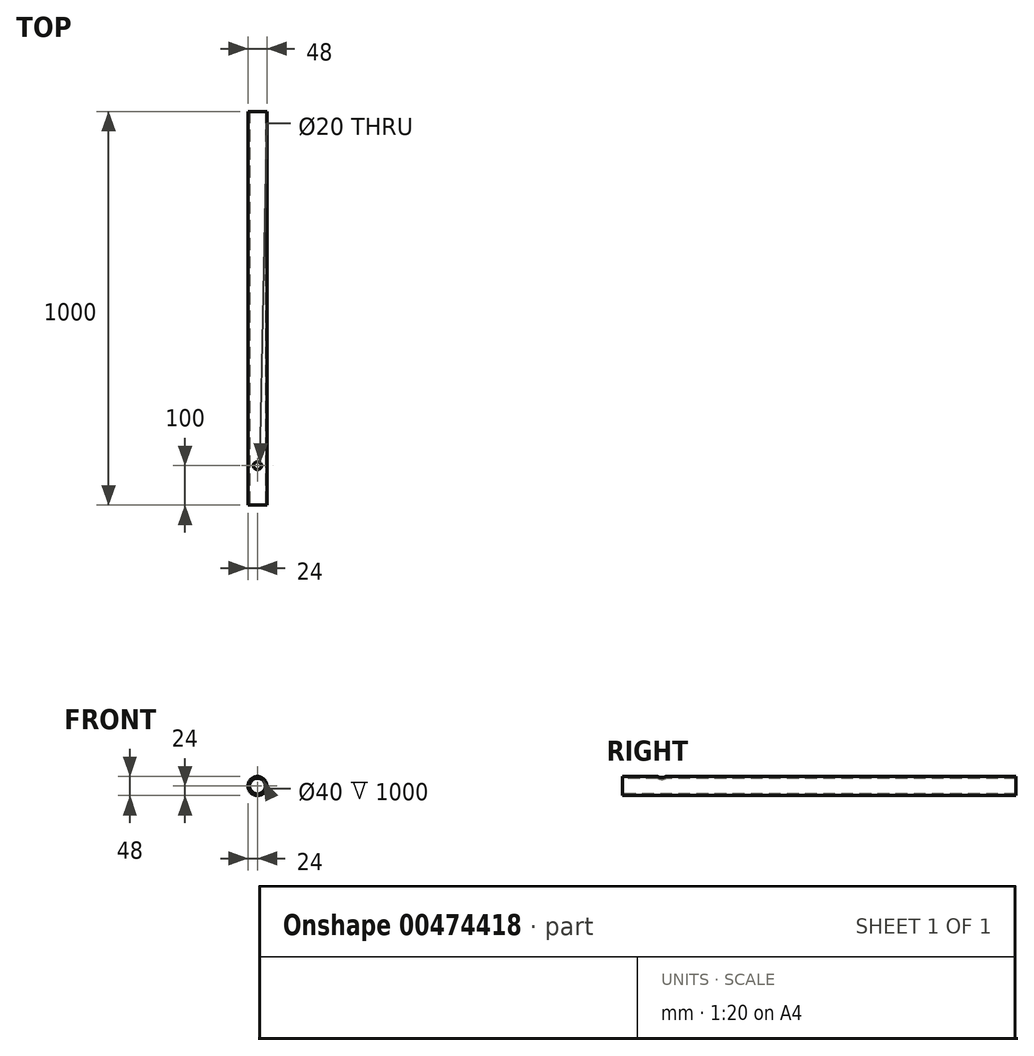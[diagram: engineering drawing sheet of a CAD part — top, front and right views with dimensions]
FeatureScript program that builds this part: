
annotation { "Feature Type Name" : "Feature", "Feature Type Description" : "" }
export const myFeature = defineFeature(function(context is Context, id is Id, definition is map)
    precondition{}
    {
        {
            var Q0;
            Q0=qCreatedBy(makeId("Front.planeOp"),FACE);
            var sketch = newSketch(context, id + "F0", { "sketchPlane" : qUnion([Q0])});
            skCircle(sketch, "E0", {"center": v(0, 0) * mm, "radius": 24 * mm});
            skSolve(sketch);
        }
        {
            var Q0;
            Q0=makeQuery(id+"F0.imprint","IMPRINT",FACE,{"disambiguationData":[TD([[makeQuery(id+"F0.imprint","IMPRINT",EDGE,{"derivedFrom":sQuery(id+"F0.wireOp",EDGE,"E0")}),1.0]])]});
            var Q1;
            Q1=sQuery(id+"F0.wireOp",EDGE,"E0");
            extrude(context, id + "F1", {"entities" : qUnion([Q0]), "surfaceEntities" : qUnion([Q1]), "oppositeDirection" : true, "depth" : 1000 * mm});
        }
        {
            var Q0;
            Q0=qCreatedBy(makeId("Front.planeOp"),FACE);
            var sketch = newSketch(context, id + "F2", { "sketchPlane" : qUnion([Q0])});
            skCircle(sketch, "E1", {"center": v(0, 0) * mm, "radius": 20 * mm});
            skSolve(sketch);
        }
        {
            var Q0;
            Q0=makeQuery(id+"F2.imprint","IMPRINT",FACE,{"disambiguationData":[TD([[makeQuery(id+"F2.imprint","IMPRINT",EDGE,{"derivedFrom":sQuery(id+"F2.wireOp",EDGE,"E1")}),1.0]])]});
            var Q1;
            Q1=sQuery(id+"F2.wireOp",EDGE,"E1");
            extrude(context, id + "F3", {"entities" : qUnion([Q0]), "operationType" : NewBodyOperationType.REMOVE, "surfaceEntities" : qUnion([Q1]), "endBound" : BoundingType.THROUGH_ALL, "oppositeDirection" : true, "depth" : 1200 * mm});
        }
        {
            var Q0;
            Q0=qCreatedBy(makeId("Top.planeOp"),FACE);
            var sketch = newSketch(context, id + "F4", { "sketchPlane" : qUnion([Q0])});
            skCircle(sketch, "E2", {"center": v(0, 100) * mm, "radius": 10 * mm});
            skSolve(sketch);
        }
        {
            var Q0;
            Q0=qSketchRegion(id+"F4",true);
            extrude(context, id + "F5", {"entities" : qUnion([Q0]), "operationType" : NewBodyOperationType.REMOVE, "depth" : 25.4 * mm});
        }
    });
